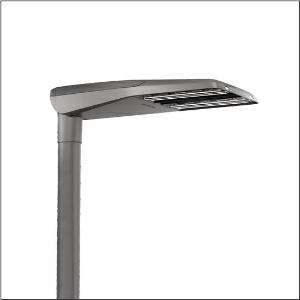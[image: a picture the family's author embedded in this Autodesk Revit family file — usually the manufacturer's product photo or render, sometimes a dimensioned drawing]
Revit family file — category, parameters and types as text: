
# Revit family: streetlight_sl_11_iq_midi___st1_2a_5xc3a51f08me_8c89
name_source: partatom
category: Lighting Fixtures
units: mm (PartAtom-declared; Revit-internal decimal feet)

## family parameters
Cut with Voids When Loaded = No
Host = Face
Light Source = No
Part Type = Normal
Room Calculation Point = No
Round Connector Dimension = Use Diameter
Shared = No

## types (1)
- --- (1 x LED, 18110 lm, 124.7 W, 3000K)
    Apparent Load = 125 VA
    CIE Flux Codes = 32 70 96 100 100
    Color Rendering = 70
    Color Temperature = 3000K
    Default Elevation = 1800 mm
    Description = Streetlight SL 11 iQ midi, mast luminaire, primary light control with 3 zone facetted reflector, of plastic, silver coated, highly specular, primary optical cover: cover, of PMMA, transparent, light distribution: ST1.2a, light emission: direct distribution, primary light characteristic: asymmetric, installation type: post-top, side-entry, LED, High Power LED, rated luminous flux: 18.110lm, luminous efficacy: 145lm/W, light colour: 730, colour temperature: 3000K, control: Street-Remote, optimised constant luminous flux control (CLO 2.0), Desk-Remote (wireless, voltage-free reading and setting of iQ features in the workshop via application-optimized NFC function/RFID function), Light-Fading, Smart-Wire, Night-Set, Lumen-Switch, Temp-Guard, Auto-Match, with cable H07RN-F 5x 1.5mm², mains connection: 230..240V, AC, 50/60Hz, connection cable pre-assembled, cable length: 12,5m, start of lifetime: 125W, end of service life: 132W, reduction: 57W, luminaire housing, of diecast aluminium, powder-coated, Siteco® metallic grey (DB 702S), please order mast flange separately, inclination adjustable without tools: 0°, 5°, 10°, 15° (post-top) | 0°, -5°, -10°, -15° (side-entry), sealing non-destructively replaceable, multi-level sealing system, length: 780mm, width: 376mm, height: 118mm, mast flange for spigot size: 42mm (side-entry): 5XC10008XM4, 60/48mm (side-entry/post-top): 5XC10108XM2, 76/60mm (side-entry/post-top): 5XC10108XM1, equipment: Power, protection rating (complete): IP66, insulation class (complete): insulation class II (safety insulation), certification: CE, ENEC, VDE, impact resistance: IK09, permissible operating ambient temperature for outdoor applications: -25..+50°C, standard-compliant lighting for roads and squares, Environmental Product Declaration (EPD) tested and certified by an independent institute, packaging unit: 1 piece

Light Distribution: ST1.2a
    Height = 118 mm
    Lamp = 1 x LED
    Lamp Light Flux = 18110 lm
    Lamp Power = 124.7 W
    Lamp count = 1
    Length = 780 mm
    Luminous efficacy = 145 lm/W
    Manufacturer = Siteco
    ModVariant = No
    Model = 5XC3A51F08ME
    Number of Poles = 1
    OnlyDefault = Yes
    Power Factor = 1
    Product Name = Streetlight SL 11 iQ midi | ST1.2a
    Product group = mast luminaire | pylon top
    ProductGroupID = 6100
    Protection Class = Protection class II
    Protection Degree = IP 66
    RLX_Detail_Level = 1
    RLX_Emergency_Light_Flux = 0 lm
    RLX_Emergency_Type = 0
    RLX_Emergency_Type_DB = No
    RlxData = <blob elided: 70765 chars, md5=6219fb1f>
    Socket = socket
    Standby Power = 0 W
    System Light Flux = 18110 lm
    System Power = 125 W
    Type Comments = factory setting: luminous flux: 100 % | dim-lin: 254 | 557 mA
    Type Image = l_1005960.jpg
    URL = http://relux.com
    VarID = @adj_131699
    Voltage = 0 V
    Weight = 0.00 kg
    Width = 376 mm

## geometry (parser evidence)
native form markers: Blend x4, Sweep x9
no freeform markers — native parametric forms only
